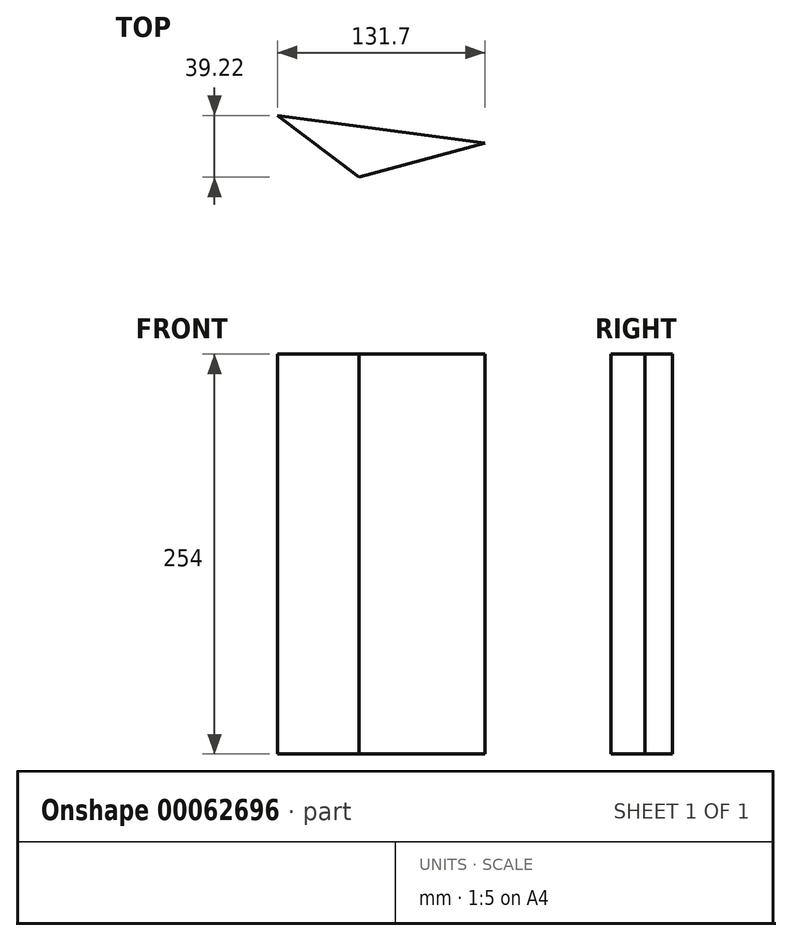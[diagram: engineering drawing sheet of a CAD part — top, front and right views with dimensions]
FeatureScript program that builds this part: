
annotation { "Feature Type Name" : "Feature", "Feature Type Description" : "" }
export const myFeature = defineFeature(function(context is Context, id is Id, definition is map)
    precondition{}
    {
        {
            var Q0;
            Q0=qCreatedBy(makeId("Top.planeOp"),FACE);
            var sketch = newSketch(context, id + "F0", { "sketchPlane" : qUnion([Q0])});
            skLineSegment(sketch, "E0", {"start": v(-162.32, 60.28) * mm, "end": v(-110.53, 21.06) * mm});
            skLineSegment(sketch, "E1", {"start": v(-110.53, 21.06) * mm, "end": v(-30.62, 42.77) * mm});
            skLineSegment(sketch, "E2", {"start": v(-30.62, 42.77) * mm, "end": v(-162.32, 60.28) * mm});
            skSolve(sketch);
        }
        {
            var Q0;
            Q0=makeQuery(id+"F0.imprint","IMPRINT",FACE,{"disambiguationData":[TD([[makeQuery(id+"F0.imprint","IMPRINT",EDGE,{"derivedFrom":sQuery(id+"F0.wireOp",EDGE,"E0")}),1.0]])]});
            extrude(context, id + "F1", {"entities" : qUnion([Q0]), "depth" : 254 * mm});
        }
    });
